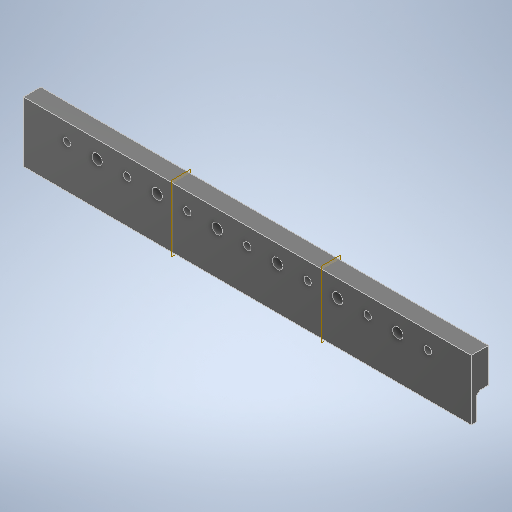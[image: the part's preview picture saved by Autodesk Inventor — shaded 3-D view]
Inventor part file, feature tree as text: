
AUTODESK INVENTOR PART (.ipt)
format: ipt  version: 2025.1 (Build 291241020, 241B)  size: 474,624 bytes
history: native  units: mm
features: sketch x5, extrude x3, hole x2, plane x2, other x2, pattern_linear x1, chamfer x1, reference x1
ambient origin geometry x8: Origin, YZ Plane, XZ Plane, XY Plane, X Axis, Y Axis, Z Axis, Center Point
bodies: Solid1 (feature_tree)
feature tree (17):
  extrude  "Extrusion1"  Depth=20.0mm
  sketch  "Sketch2"  dims[d2=3.0mm d3=0.0mm d5=25.4mm]
  extrude  "Extrusion3"  Depth=3.0mm
  hole  "Hole2"  [1 undecoded]
  hole  "Hole3"  [1 undecoded]
  pattern_linear  "Rectangular Pattern2"  Spacing1=42.6875mm  [1 undecoded]
  chamfer  "Chamfer1"  Distance=34.925mm
  extrude  "Extrusion4"  Depth=5.0mm
  plane  "Work Plane1"
  plane  "Work Plane2"
  sketch  "Sketch1"  dims[d0=260.0mm d1=20.0mm]
  reference  "Reference1"
  sketch  "Sketch5"  dims[d6=12.7mm d31=10.0mm]
  sketch  "Sketch6"  dims[d32=20.0mm d33=10.0mm d34=0.0mm]
  sketch  "Sketch7"  dims[d35=42.6875mm d39=6.0mm d40=6.0mm d41=4.0mm d42=2.0mm d43=90.0deg d44=8.0mm d45=20.594885mm d46=42.6875mm d47=34.925mm d48=34.925mm d49=34.925mm d50=34.925mm d51=10.0mm d52=4.3mm d53=6.0mm d54=4.0mm d55=2.0mm d56=90.0deg d57=6.0mm d58=0.0mm d59=70.0mm d61=34.925mm d62=10.0mm d63=2.0mm d64=2.0mm d65=45.0deg d66=5.0mm d67=0.0mm d68=0.0mm d69=-86.666667mm d70=-173.333333mm]
  other  "MagDrop4.iam"
  other  "Connect4_RACK:1"
note: 3 required parameter values undecoded (feature->parameter linkage not recoverable at this tier; creation-order binding heuristic only, values carry confidence <= 0.55)
